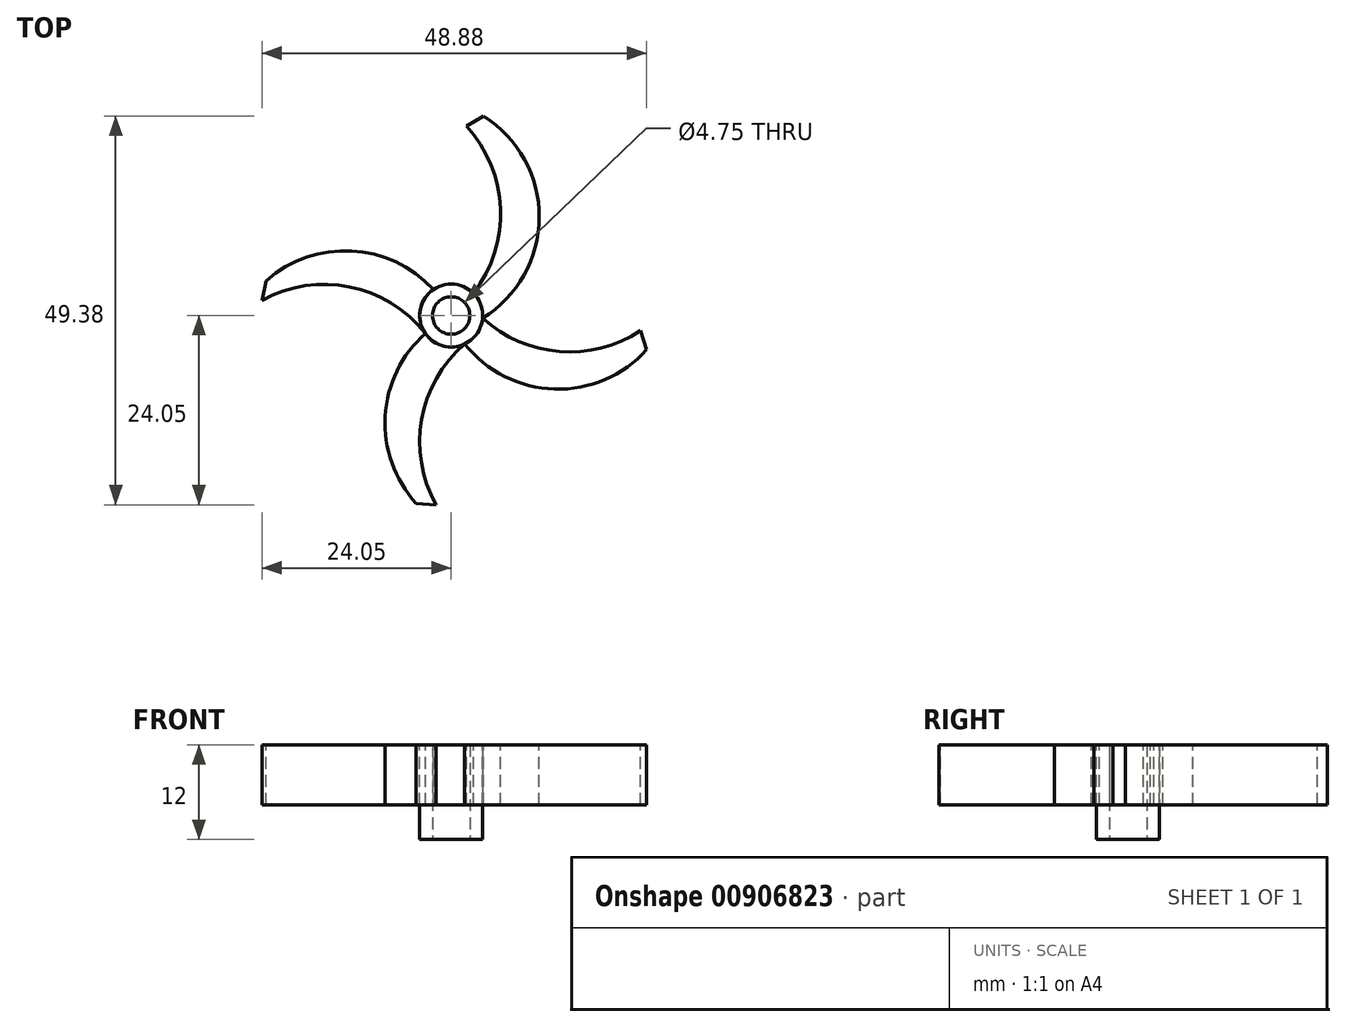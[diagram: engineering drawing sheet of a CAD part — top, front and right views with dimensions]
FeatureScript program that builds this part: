
annotation { "Feature Type Name" : "Feature", "Feature Type Description" : "" }
export const myFeature = defineFeature(function(context is Context, id is Id, definition is map)
    precondition{}
    {
        {
            var Q0;
            Q0=qCreatedBy(makeId("Top.planeOp"),FACE);
            var sketch = newSketch(context, id + "F0", { "sketchPlane" : qUnion([Q0])});
            skCircle(sketch, "E0", {"center": v(0, 0) * mm, "radius": 2.38 * mm});
            skCircle(sketch, "E1", {"center": v(0, 0) * mm, "radius": 4 * mm});
            skSolve(sketch);
        }
        {
            var Q0;
            Q0=makeQuery(id+"F0.imprint","IMPRINT",FACE,{"disambiguationData":[TD([[makeQuery(id+"F0.imprint","IMPRINT",EDGE,{"derivedFrom":sQuery(id+"F0.wireOp",EDGE,"E0")}),-1.0]])]});
            extrude(context, id + "F1", {"entities" : qUnion([Q0]), "depth" : 12 * mm, "offsetDistance" : 25.4 * mm, "symmetric" : true});
        }
        {
            var Q0;
            Q0=makeQuery(id+"F1.opExtrude","CAP_FACE",FACE,{"disambiguationData":[OSD([sQuery(id+"F0.wireOp",EDGE,"E0"),sQuery(id+"F0.wireOp",EDGE,"E1")])],"isStart":false});
            var sketch = newSketch(context, id + "F2", { "sketchPlane" : qUnion([Q0])});
            skLineSegment(sketch, "E2", {"start": v(0, 0) * mm, "end": v(1.92, 24.05) * mm, "construction": true});
            skLineSegment(sketch, "E3", {"start": v(0, 0) * mm, "end": v(24.05, -1.92) * mm, "construction": true});
            skLineSegment(sketch, "E4", {"start": v(0, 0) * mm, "end": v(-1.92, -24.05) * mm, "construction": true});
            skLineSegment(sketch, "E5", {"start": v(0, 0) * mm, "end": v(-24.05, 1.92) * mm, "construction": true});
            skArc(sketch, "E6", {"start": v(2.82, 2.83) * mm, "mid": v(6.27, 13.6) * mm, "end": v(1.92, 24.05) * mm});
            skLineSegment(sketch, "E7", {"start": v(1.92, 24.05) * mm, "end": v(4.12, 25.33) * mm});
            skArc(sketch, "E8", {"start": v(3.98, -0.35) * mm, "mid": v(11.18, 12.46) * mm, "end": v(4.12, 25.33) * mm});
            skArc(sketch, "E9", {"start": v(3.98, -0.35) * mm, "mid": v(3.7, 1.35) * mm, "end": v(2.82, 2.83) * mm});
            skLineSegment(sketch, "E10", {"start": v(24.05, -1.92) * mm, "end": v(24.83, -4.34) * mm});
            skArc(sketch, "E11", {"start": v(3.98, -0.35) * mm, "mid": v(13.75, -4.57) * mm, "end": v(24.05, -1.92) * mm});
            skArc(sketch, "E12", {"start": v(1.71, -3.61) * mm, "mid": v(13.1, -9.35) * mm, "end": v(24.83, -4.34) * mm});
            skArc(sketch, "E13", {"start": v(1.71, -3.61) * mm, "mid": v(3.21, -2.23) * mm, "end": v(3.98, -0.35) * mm});
            skArc(sketch, "E14", {"start": v(1.71, -3.61) * mm, "mid": v(-3.75, -13.19) * mm, "end": v(-1.92, -24.05) * mm});
            skLineSegment(sketch, "E15", {"start": v(-1.92, -24.05) * mm, "end": v(-4.46, -23.85) * mm});
            skArc(sketch, "E16", {"start": v(-3.28, -2.29) * mm, "mid": v(-8.39, -12.82) * mm, "end": v(-4.46, -23.85) * mm});
            skArc(sketch, "E17", {"start": v(-3.28, -2.29) * mm, "mid": v(-1, -3.74) * mm, "end": v(1.71, -3.61) * mm});
            skArc(sketch, "E18", {"start": v(-3.28, -2.29) * mm, "mid": v(-12.9, 3.62) * mm, "end": v(-24.05, 1.92) * mm});
            skArc(sketch, "E19", {"start": v(-2.27, 3.3) * mm, "mid": v(-12.67, 8.2) * mm, "end": v(-23.52, 4.4) * mm});
            skLineSegment(sketch, "E20", {"start": v(-24.05, 1.92) * mm, "end": v(-23.52, 4.4) * mm});
            skSolve(sketch);
        }
        {
            var Q0;
            {var subQ0=sQuery(id+"F2.wireOp",EDGE,"E14");Q0=makeQuery(id+"F2.imprint","IMPRINT",FACE,{"disambiguationData":[TD([[makeQuery(id+"F2.imprint","IMPRINT",EDGE,{"derivedFrom":subQ0}),-1.0]])]});}
            var Q1;
            {var subQ0=sQuery(id+"F2.wireOp",EDGE,"E18");Q1=makeQuery(id+"F2.imprint","IMPRINT",FACE,{"disambiguationData":[TD([[makeQuery(id+"F2.imprint","IMPRINT",EDGE,{"derivedFrom":subQ0}),-1.0]])]});}
            var Q2;
            {var subQ0=sQuery(id+"F2.wireOp",EDGE,"E6");Q2=makeQuery(id+"F2.imprint","IMPRINT",FACE,{"disambiguationData":[TD([[makeQuery(id+"F2.imprint","IMPRINT",EDGE,{"derivedFrom":subQ0}),-1.0]])]});}
            var Q3;
            Q3=makeQuery(id+"F2.imprint","IMPRINT",FACE,{"disambiguationData":[TD([[makeQuery(id+"F2.imprint","IMPRINT",EDGE,{"derivedFrom":sQuery(id+"F2.wireOp",EDGE,"E10")}),-1.0]])]});
            extrude(context, id + "F3", {"entities" : qUnion([Q0, Q1, Q2, Q3]), "oppositeDirection" : true, "depth" : 7.62 * mm, "offsetDistance" : 25.4 * mm});
        }
    });
